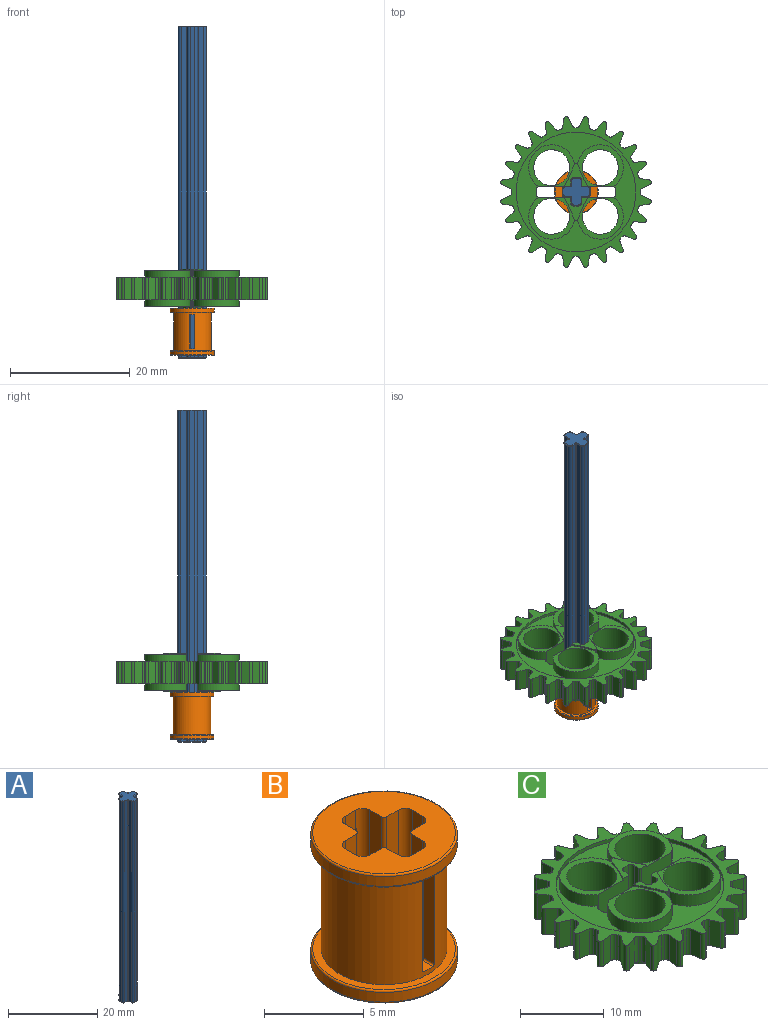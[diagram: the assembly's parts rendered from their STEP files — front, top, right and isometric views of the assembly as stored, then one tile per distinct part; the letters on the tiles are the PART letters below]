
ASSEMBLY  parts=3 mates=2
PART A: 74 faces, bbox 4.8x4.8x55.5 mm
  f0: cylinder r=0.1mm len=55.3mm, axis (0,0,-1), area 8.7mm2, adj f1,f23,f46,f70
  f1: plane 55.3x0.88mm, normal (1,0,0), area 48.4mm2, adj f0,f2,f44,f68
  f2: cylinder r=0.5mm len=55.3mm, axis (0,0,-1), area 43.4mm2, adj f1,f3,f42,f66
  f3: plane 55.3x0.75mm, normal (0,1,0), area 41.5mm2, adj f2,f4,f40,f64
  f4: cylinder r=0.5mm len=55.3mm, axis (0,0,-1), area 43.4mm2, adj f3,f5,f38,f62
  f5: plane 55.3x0.88mm, normal (-1,0,0), area 48.4mm2, adj f4,f6,f36,f60
  f6: cylinder r=0.1mm len=55.3mm, axis (0,0,-1), area 8.7mm2, adj f5,f7,f34,f58
  f7: plane 55.3x0.88mm, normal (0,1,0), area 48.4mm2, adj f6,f8,f32,f56
  f8: cylinder r=0.5mm len=55.3mm, axis (0,0,-1), area 43.4mm2, adj f7,f9,f30,f54
  f9: plane 55.3x0.75mm, normal (-1,0,0), area 41.5mm2, adj f8,f10,f28,f52
  f10: cylinder r=0.5mm len=55.3mm, axis (0,0,-1), area 43.4mm2, adj f9,f11,f26,f50
  f11: plane 55.3x0.88mm, normal (0,-1,0), area 48.4mm2, adj f10,f12,f27,f51
  f12: cylinder r=0.1mm len=55.3mm, axis (0,0,-1), area 8.7mm2, adj f11,f13,f29,f53
  f13: plane 55.3x0.88mm, normal (-1,0,0), area 48.4mm2, adj f12,f14,f31,f55
  f14: cylinder r=0.5mm len=55.3mm, axis (0,0,-1), area 43.4mm2, adj f13,f15,f33,f57
  f15: plane 55.3x0.75mm, normal (0,-1,0), area 41.5mm2, adj f14,f16,f35,f59
  f16: cylinder r=0.5mm len=55.3mm, axis (0,0,-1), area 43.4mm2, adj f15,f17,f37,f61
  f17: plane 55.3x0.88mm, normal (1,0,0), area 48.4mm2, adj f16,f18,f39,f63
  f18: cylinder r=0.1mm len=55.3mm, axis (0,0,-1), area 8.7mm2, adj f17,f19,f41,f65
  f19: plane 55.3x0.88mm, normal (0,-1,0), area 48.4mm2, adj f18,f20,f43,f67
  f20: cylinder r=0.5mm len=55.3mm, axis (0,0,-1), area 43.4mm2, adj f19,f21,f45,f69
  f21: plane 55.3x0.75mm, normal (1,0,0), area 41.5mm2, adj f20,f22,f47,f71
  f22: cylinder r=0.5mm len=55.3mm, axis (0,0,-1), area 43.4mm2, adj f21,f23,f49,f73
  f23: plane 55.3x0.88mm, normal (0,1,0), area 48.4mm2, adj f0,f22,f48,f72
  f24: plane 4.5x4.5mm, normal (0,0,1), area 11.3mm2, adj f50,f51,f52,f53,f54,f55,f56,f57
  f25: plane 4.5x4.5mm, normal (0,0,-1), area 11.3mm2, adj f26,f27,f28,f29,f30,f31,f32,f33
  f26: torus R=0.4mm, axis (0,0,1), area 0.1mm2, adj f10,f25,f27,f28
  f27: cylinder r=0.1mm len=0.88mm, axis (1,0,0), area 0.1mm2, adj f11,f25,f26,f29
  f28: cylinder r=0.1mm len=0.75mm, axis (0,-1,0), area 0.1mm2, adj f9,f25,f26,f30
  f29: torus R=0.2mm, axis (0,0,1), area 0mm2, adj f12,f25,f27,f31
  f30: torus R=0.4mm, axis (0,0,1), area 0.1mm2, adj f8,f25,f28,f32
  f31: cylinder r=0.1mm len=0.88mm, axis (0,-1,0), area 0.1mm2, adj f13,f25,f29,f33
  f32: cylinder r=0.1mm len=0.88mm, axis (-1,0,0), area 0.1mm2, adj f7,f25,f30,f34
  f33: torus R=0.4mm, axis (0,0,1), area 0.1mm2, adj f14,f25,f31,f35
  f34: torus R=0.2mm, axis (0,0,1), area 0mm2, adj f6,f25,f32,f36
  f35: cylinder r=0.1mm len=0.75mm, axis (1,0,0), area 0.1mm2, adj f15,f25,f33,f37
  f36: cylinder r=0.1mm len=0.88mm, axis (0,-1,0), area 0.1mm2, adj f5,f25,f34,f38
  f37: torus R=0.4mm, axis (0,0,1), area 0.1mm2, adj f16,f25,f35,f39
  f38: torus R=0.4mm, axis (0,0,1), area 0.1mm2, adj f4,f25,f36,f40
  f39: cylinder r=0.1mm len=0.88mm, axis (0,1,0), area 0.1mm2, adj f17,f25,f37,f41
  f40: cylinder r=0.1mm len=0.75mm, axis (-1,0,0), area 0.1mm2, adj f3,f25,f38,f42
  f41: torus R=0.2mm, axis (0,0,1), area 0mm2, adj f18,f25,f39,f43
  f42: torus R=0.4mm, axis (0,0,1), area 0.1mm2, adj f2,f25,f40,f44
  f43: cylinder r=0.1mm len=0.88mm, axis (1,0,0), area 0.1mm2, adj f19,f25,f41,f45
  f44: cylinder r=0.1mm len=0.88mm, axis (0,1,0), area 0.1mm2, adj f1,f25,f42,f46
  f45: torus R=0.4mm, axis (0,0,1), area 0.1mm2, adj f20,f25,f43,f47
  f46: torus R=0.2mm, axis (0,0,1), area 0mm2, adj f0,f25,f44,f48
  f47: cylinder r=0.1mm len=0.75mm, axis (0,1,0), area 0.1mm2, adj f21,f25,f45,f49
  f48: cylinder r=0.1mm len=0.88mm, axis (-1,0,0), area 0.1mm2, adj f23,f25,f46,f49
  f49: torus R=0.4mm, axis (0,0,1), area 0.1mm2, adj f22,f25,f47,f48
  f50: torus R=0.4mm, axis (0,0,1), area 0.1mm2, adj f10,f24,f51,f52
  f51: cylinder r=0.1mm len=0.88mm, axis (-1,0,0), area 0.1mm2, adj f11,f24,f50,f53
  f52: cylinder r=0.1mm len=0.75mm, axis (0,1,0), area 0.1mm2, adj f9,f24,f50,f54
  f53: torus R=0.2mm, axis (0,0,1), area 0mm2, adj f12,f24,f51,f55
  f54: torus R=0.4mm, axis (0,0,1), area 0.1mm2, adj f8,f24,f52,f56
  f55: cylinder r=0.1mm len=0.88mm, axis (0,1,0), area 0.1mm2, adj f13,f24,f53,f57
  f56: cylinder r=0.1mm len=0.88mm, axis (1,0,0), area 0.1mm2, adj f7,f24,f54,f58
  f57: torus R=0.4mm, axis (0,0,1), area 0.1mm2, adj f14,f24,f55,f59
  f58: torus R=0.2mm, axis (0,0,1), area 0mm2, adj f6,f24,f56,f60
  f59: cylinder r=0.1mm len=0.75mm, axis (-1,0,0), area 0.1mm2, adj f15,f24,f57,f61
  f60: cylinder r=0.1mm len=0.88mm, axis (0,1,0), area 0.1mm2, adj f5,f24,f58,f62
  f61: torus R=0.4mm, axis (0,0,1), area 0.1mm2, adj f16,f24,f59,f63
  f62: torus R=0.4mm, axis (0,0,1), area 0.1mm2, adj f4,f24,f60,f64
  f63: cylinder r=0.1mm len=0.88mm, axis (0,-1,0), area 0.1mm2, adj f17,f24,f61,f65
  f64: cylinder r=0.1mm len=0.75mm, axis (1,0,0), area 0.1mm2, adj f3,f24,f62,f66
  f65: torus R=0.2mm, axis (0,0,1), area 0mm2, adj f18,f24,f63,f67
  f66: torus R=0.4mm, axis (0,0,1), area 0.1mm2, adj f2,f24,f64,f68
  f67: cylinder r=0.1mm len=0.88mm, axis (-1,0,0), area 0.1mm2, adj f19,f24,f65,f69
  f68: cylinder r=0.1mm len=0.88mm, axis (0,-1,0), area 0.1mm2, adj f1,f24,f66,f70
  f69: torus R=0.4mm, axis (0,0,1), area 0.1mm2, adj f20,f24,f67,f71
  f70: torus R=0.2mm, axis (0,0,1), area 0mm2, adj f0,f24,f68,f72
  f71: cylinder r=0.1mm len=0.75mm, axis (0,-1,0), area 0.1mm2, adj f21,f24,f69,f73
  f72: cylinder r=0.1mm len=0.88mm, axis (1,0,0), area 0.1mm2, adj f23,f24,f70,f73
  f73: torus R=0.4mm, axis (0,0,1), area 0.1mm2, adj f22,f24,f71,f72
PART B: 53 faces, bbox 8x8x7.9 mm
  f0: plane 1.11x0.75mm, normal (0,1,0), area 0.8mm2, adj f13,f15,f30,f39,f40,f41
  f1: plane 1.11x0.75mm, normal (0,-1,0), area 0.8mm2, adj f25,f28,f30,f46,f47,f51
  f2: cylinder r=3.15mm len=6.3mm, axis (0,0,1), area 115mm2, adj f31,f32,f37,f38,f39,f40,f41,f42
  f3: cylinder r=3.67mm len=7.35mm, axis (0,0,-1), area 13.9mm2, adj f34,f35
  f4: plane 7.9x0.8mm, normal (-1,0,0), area 6.3mm2, adj f5,f28,f29,f30
  f5: cylinder r=0.2mm len=7.9mm, axis (0,0,-1), area 2.5mm2, adj f4,f6,f29,f30
  f6: plane 7.9x0.8mm, normal (0,-1,0), area 6.3mm2, adj f5,f7,f29,f30
  f7: cylinder r=0.5mm len=7.9mm, axis (0,0,-1), area 6.2mm2, adj f6,f8,f29,f30
  f8: plane 7.9x0.75mm, normal (-1,0,0), area 5.9mm2, adj f7,f9,f29,f30
  f9: cylinder r=0.5mm len=7.9mm, axis (0,0,-1), area 6.2mm2, adj f8,f10,f29,f30
  f10: plane 7.9x0.8mm, normal (0,1,0), area 6.3mm2, adj f9,f11,f29,f30
  f11: cylinder r=0.2mm len=7.9mm, axis (0,0,-1), area 2.5mm2, adj f10,f12,f29,f30
  f12: plane 7.9x0.8mm, normal (-1,0,0), area 6.3mm2, adj f11,f13,f29,f30
  f13: cylinder r=0.5mm len=7.9mm, axis (0,0,-1), area 5.9mm2, adj f0,f12,f14,f29,f30,f37,f38,f39
  f14: plane 1.11x0.75mm, normal (0,1,0), area 0.8mm2, adj f13,f15,f29,f37,f43,f44
  f15: cylinder r=0.5mm len=7.9mm, axis (0,0,-1), area 5.9mm2, adj f0,f14,f16,f29,f30,f41,f42,f43
  f16: plane 7.9x0.8mm, normal (1,0,0), area 6.3mm2, adj f15,f17,f29,f30
  f17: cylinder r=0.2mm len=7.9mm, axis (0,0,-1), area 2.5mm2, adj f16,f18,f29,f30
  f18: plane 7.9x0.8mm, normal (0,1,0), area 6.3mm2, adj f17,f19,f29,f30
  f19: cylinder r=0.5mm len=7.9mm, axis (0,0,-1), area 6.2mm2, adj f18,f20,f29,f30
  f20: plane 7.9x0.75mm, normal (1,0,0), area 5.9mm2, adj f19,f21,f29,f30
  f21: cylinder r=0.5mm len=7.9mm, axis (0,0,-1), area 6.2mm2, adj f20,f22,f29,f30
  f22: plane 7.9x0.8mm, normal (0,-1,0), area 6.3mm2, adj f21,f23,f29,f30
  f23: cylinder r=0.2mm len=7.9mm, axis (0,0,-1), area 2.5mm2, adj f22,f24,f29,f30
  f24: plane 7.9x0.8mm, normal (1,0,0), area 6.3mm2, adj f23,f25,f29,f30
  f25: cylinder r=0.5mm len=7.9mm, axis (0,0,-1), area 5.9mm2, adj f1,f24,f26,f29,f30,f49,f50,f51
  f26: plane 1.11x0.75mm, normal (0,-1,0), area 0.8mm2, adj f25,f28,f29,f45,f48,f49
  f27: cylinder r=3.67mm len=7.35mm, axis (0,0,-1), area 13.9mm2, adj f33,f36
  f28: cylinder r=0.5mm len=7.9mm, axis (0,0,-1), area 5.9mm2, adj f1,f4,f26,f29,f30,f47,f48,f52
  f29: plane 7.15x7.15mm, normal (0,0,1), area 27mm2, adj f4,f5,f6,f7,f8,f9,f10,f11
  f30: plane 7.15x7.15mm, normal (0,0,-1), area 27mm2, adj f0,f1,f4,f5,f6,f7,f8,f9
  f31: plane 7.15x7.15mm, normal (0,0,-1), area 9mm2, adj f2,f33
  f32: plane 7.15x7.15mm, normal (0,0,1), area 9mm2, adj f2,f34
  f33: torus R=3.58mm, axis (0,0,1), area 3.6mm2, adj f27,f31
  f34: torus R=3.58mm, axis (0,0,1), area 3.6mm2, adj f3,f32
  f35: torus R=3.58mm, axis (0,0,1), area 3.6mm2, adj f3,f30
  f36: torus R=3.58mm, axis (0,0,1), area 3.6mm2, adj f27,f29
  f37: cylinder r=0.1mm len=0.76mm, axis (0,-1,0), area 0.1mm2, adj f2,f13,f14,f38,f44
  f38: plane 5.5x0.75mm, normal (-1,0,0), area 4.1mm2, adj f2,f13,f37,f39
  f39: cylinder r=0.1mm len=0.76mm, axis (0,-1,0), area 0.1mm2, adj f0,f2,f13,f38,f40
  f40: plane 0.78x0.65mm, normal (0,0,1), area 0.5mm2, adj f0,f2,f39,f41
  f41: cylinder r=0.1mm len=0.76mm, axis (0,-1,0), area 0.1mm2, adj f0,f2,f15,f40,f42
  f42: plane 5.5x0.75mm, normal (1,0,0), area 4.1mm2, adj f2,f15,f41,f43
  f43: cylinder r=0.1mm len=0.76mm, axis (0,-1,0), area 0.1mm2, adj f2,f14,f15,f42,f44
  f44: plane 0.78x0.65mm, normal (0,0,-1), area 0.5mm2, adj f2,f14,f37,f43
  f45: plane 0.78x0.65mm, normal (0,0,-1), area 0.5mm2, adj f2,f26,f48,f49
  f46: plane 0.78x0.65mm, normal (0,0,1), area 0.5mm2, adj f1,f2,f47,f51
  f47: cylinder r=0.1mm len=0.76mm, axis (0,-1,0), area 0.1mm2, adj f1,f2,f28,f46,f52
  f48: cylinder r=0.1mm len=0.76mm, axis (0,-1,0), area 0.1mm2, adj f2,f26,f28,f45,f52
  f49: cylinder r=0.1mm len=0.76mm, axis (0,-1,0), area 0.1mm2, adj f2,f25,f26,f45,f50
  f50: plane 5.5x0.75mm, normal (1,0,0), area 4.1mm2, adj f2,f25,f49,f51
  f51: cylinder r=0.1mm len=0.76mm, axis (0,-1,0), area 0.1mm2, adj f1,f2,f25,f46,f50
  f52: plane 5.5x0.75mm, normal (-1,0,0), area 4.1mm2, adj f2,f28,f47,f48
PART C: 242 faces, bbox 25.3x25.3x6.5 mm
  f0: plane 7.61x7.02mm, normal (0,0,-1), area 14.5mm2, adj f4,f189,f190,f212,f222,f228
  f1: plane 7.61x7.02mm, normal (0,0,1), area 14.5mm2, adj f3,f190,f191,f203,f222,f228
  f2: plane 3.93x3.88mm, normal (0,0,1), area 5.4mm2, adj f3,f199,f202,f203,f206,f224,f225,f226
  f3: cylinder r=20mm len=3.7mm, axis (0,0,-1), area 1mm2, adj f1,f2,f203,f228
  f4: cylinder r=20mm len=3.7mm, axis (0,0,-1), area 1mm2, adj f0,f5,f212,f228
  f5: plane 3.93x3.88mm, normal (0,0,-1), area 5.4mm2, adj f4,f209,f210,f211,f212,f224,f225,f226
  f6: plane 20x20mm, normal (0,0,1), area 104.2mm2, adj f12,f17,f188,f191,f196,f199,f201,f203
  f7: plane 20x20mm, normal (0,0,-1), area 104.2mm2, adj f11,f16,f186,f189,f194,f208,f209,f211
  f8: plane 7.61x7.02mm, normal (0,0,-1), area 14.5mm2, adj f186,f187,f210,f211,f221,f238
  f9: plane 7.61x7.02mm, normal (0,0,1), area 14.5mm2, adj f187,f188,f199,f202,f221,f238
  f10: plane 7.61x7.02mm, normal (0,0,-1), area 14.5mm2, adj f11,f192,f213,f214,f220,f229
  f11: cylinder r=3.82mm len=7.61mm, axis (0,0,-1), area 24.7mm2, adj f7,f10,f214,f220
  f12: cylinder r=3.82mm len=7.61mm, axis (0,0,-1), area 24.7mm2, adj f6,f13,f204,f220
  f13: plane 7.61x7.02mm, normal (0,0,1), area 14.5mm2, adj f12,f192,f204,f205,f220,f229
  f14: plane 25.27x25.27mm, normal (0,0,1), area 106.3mm2, adj f17,f18,f19,f20,f21,f22,f23,f24
  f15: plane 25.27x25.27mm, normal (0,0,-1), area 106.3mm2, adj f16,f18,f19,f20,f21,f22,f23,f24
  f16: cylinder r=10mm len=20mm, axis (0,0,-1), area 31.4mm2, adj f7,f15
  f17: cylinder r=10mm len=20mm, axis (0,0,-1), area 31.4mm2, adj f6,f14
  f18: cylinder r=0.5mm len=3.75mm, axis (0,0,1), area 2.1mm2, adj f14,f15,f19,f185
  f19: cylinder r=0.5mm len=3.75mm, axis (0,0,1), area 2.1mm2, adj f14,f15,f18,f20
  f20: plane 3.75x1.41mm, normal (0.99,0.16,0), area 5.3mm2, adj f14,f15,f19,f21
  f21: cylinder r=0.5mm len=3.75mm, axis (0,0,1), area 2.1mm2, adj f14,f15,f20,f22
  f22: plane 3.75x0.34mm, normal (0.26,0.97,0), area 1.3mm2, adj f14,f15,f21,f23
  f23: cylinder r=0.5mm len=3.75mm, axis (0,0,1), area 2.1mm2, adj f14,f15,f22,f24
  f24: plane 3.75x1.1mm, normal (-0.77,0.64,0), area 5.3mm2, adj f14,f15,f23,f25
  f25: cylinder r=0.5mm len=3.75mm, axis (0,0,1), area 2.1mm2, adj f14,f15,f24,f26
  f26: cylinder r=0.5mm len=3.75mm, axis (0,0,1), area 2.1mm2, adj f14,f15,f25,f27
  f27: plane 3.75x1.42mm, normal (1,-0.1,0), area 5.3mm2, adj f14,f15,f26,f28
  f28: cylinder r=0.5mm len=3.75mm, axis (0,0,1), area 2.1mm2, adj f14,f15,f27,f29
  f29: plane 3.75x0.31mm, normal (0.5,0.87,0), area 1.3mm2, adj f14,f15,f28,f30
  f30: cylinder r=0.5mm len=3.75mm, axis (0,0,1), area 2.1mm2, adj f14,f15,f29,f31
  f31: plane 3.75x1.16mm, normal (-0.58,0.81,0), area 5.3mm2, adj f14,f15,f30,f32
  f32: cylinder r=0.5mm len=3.75mm, axis (0,0,1), area 2.1mm2, adj f14,f15,f31,f33
  f33: cylinder r=0.5mm len=3.75mm, axis (0,0,1), area 2.1mm2, adj f14,f15,f32,f34
  f34: plane 3.75x1.34mm, normal (0.94,-0.35,0), area 5.3mm2, adj f14,f15,f33,f35
  f35: cylinder r=0.5mm len=3.75mm, axis (0,0,1), area 2.1mm2, adj f14,f15,f34,f36
  f36: plane 3.75x0.25mm, normal (0.71,0.71,0), area 1.3mm2, adj f14,f15,f35,f37
  f37: cylinder r=0.5mm len=3.75mm, axis (0,0,1), area 2.1mm2, adj f14,f15,f36,f38
  f38: plane 3.75x1.34mm, normal (-0.35,0.94,0), area 5.3mm2, adj f14,f15,f37,f39
  f39: cylinder r=0.5mm len=3.75mm, axis (0,0,1), area 2.1mm2, adj f14,f15,f38,f40
  f40: cylinder r=0.5mm len=3.75mm, axis (0,0,1), area 2.1mm2, adj f14,f15,f39,f41
  f41: plane 3.75x1.16mm, normal (0.81,-0.58,0), area 5.3mm2, adj f14,f15,f40,f42
  f42: cylinder r=0.5mm len=3.75mm, axis (0,0,1), area 2.1mm2, adj f14,f15,f41,f43
  f43: plane 3.75x0.31mm, normal (0.87,0.5,0), area 1.3mm2, adj f14,f15,f42,f44
  f44: cylinder r=0.5mm len=3.75mm, axis (0,0,1), area 2.1mm2, adj f14,f15,f43,f45
  f45: plane 3.75x1.42mm, normal (-0.1,1,0), area 5.3mm2, adj f14,f15,f44,f46
  f46: cylinder r=0.5mm len=3.75mm, axis (0,0,1), area 2.1mm2, adj f14,f15,f45,f47
  f47: cylinder r=0.5mm len=3.75mm, axis (0,0,1), area 2.1mm2, adj f14,f15,f46,f48
  f48: plane 3.75x1.1mm, normal (0.64,-0.77,0), area 5.3mm2, adj f14,f15,f47,f49
  f49: cylinder r=0.5mm len=3.75mm, axis (0,0,1), area 2.1mm2, adj f14,f15,f48,f50
  f50: plane 3.75x0.34mm, normal (0.97,0.26,0), area 1.3mm2, adj f14,f15,f49,f51
  f51: cylinder r=0.5mm len=3.75mm, axis (0,0,1), area 2.1mm2, adj f14,f15,f50,f52
  f52: plane 3.75x1.41mm, normal (0.16,0.99,0), area 5.3mm2, adj f14,f15,f51,f53
  f53: cylinder r=0.5mm len=3.75mm, axis (0,0,1), area 2.1mm2, adj f14,f15,f52,f54
  f54: cylinder r=0.5mm len=3.75mm, axis (0,0,1), area 2.1mm2, adj f14,f15,f53,f55
  f55: plane 3.75x1.3mm, normal (0.41,-0.91,0), area 5.3mm2, adj f14,f15,f54,f56
  f56: cylinder r=0.5mm len=3.75mm, axis (0,0,1), area 2.1mm2, adj f14,f15,f55,f57
  f57: plane 3.75x0.36mm, normal (1,0,0), area 1.3mm2, adj f14,f15,f56,f58
  f58: cylinder r=0.5mm len=3.75mm, axis (0,0,1), area 2.1mm2, adj f14,f15,f57,f59
  f59: plane 3.75x1.3mm, normal (0.41,0.91,0), area 5.3mm2, adj f14,f15,f58,f60
  f60: cylinder r=0.5mm len=3.75mm, axis (0,0,1), area 2.1mm2, adj f14,f15,f59,f61
  f61: cylinder r=0.5mm len=3.75mm, axis (0,0,1), area 2.1mm2, adj f14,f15,f60,f62
  f62: plane 3.75x1.41mm, normal (0.16,-0.99,0), area 5.3mm2, adj f14,f15,f61,f63
  f63: cylinder r=0.5mm len=3.75mm, axis (0,0,1), area 2.1mm2, adj f14,f15,f62,f64
  f64: plane 3.75x0.34mm, normal (0.97,-0.26,0), area 1.3mm2, adj f14,f15,f63,f65
  f65: cylinder r=0.5mm len=3.75mm, axis (0,0,1), area 2.1mm2, adj f14,f15,f64,f66
  f66: plane 3.75x1.1mm, normal (0.64,0.77,0), area 5.3mm2, adj f14,f15,f65,f67
  f67: cylinder r=0.5mm len=3.75mm, axis (0,0,1), area 2.1mm2, adj f14,f15,f66,f68
  f68: cylinder r=0.5mm len=3.75mm, axis (0,0,1), area 2.1mm2, adj f14,f15,f67,f69
  f69: plane 3.75x1.42mm, normal (-0.1,-1,0), area 5.3mm2, adj f14,f15,f68,f70
  f70: cylinder r=0.5mm len=3.75mm, axis (0,0,1), area 2.1mm2, adj f14,f15,f69,f71
  f71: plane 3.75x0.31mm, normal (0.87,-0.5,0), area 1.3mm2, adj f14,f15,f70,f72
  f72: cylinder r=0.5mm len=3.75mm, axis (0,0,1), area 2.1mm2, adj f14,f15,f71,f73
  f73: plane 3.75x1.16mm, normal (0.81,0.58,0), area 5.3mm2, adj f14,f15,f72,f74
  f74: cylinder r=0.5mm len=3.75mm, axis (0,0,1), area 2.1mm2, adj f14,f15,f73,f75
  f75: cylinder r=0.5mm len=3.75mm, axis (0,0,1), area 2.1mm2, adj f14,f15,f74,f76
  f76: plane 3.75x1.34mm, normal (-0.35,-0.94,0), area 5.3mm2, adj f14,f15,f75,f77
  f77: cylinder r=0.5mm len=3.75mm, axis (0,0,1), area 2.1mm2, adj f14,f15,f76,f78
  f78: plane 3.75x0.25mm, normal (0.71,-0.71,0), area 1.3mm2, adj f14,f15,f77,f79
  f79: cylinder r=0.5mm len=3.75mm, axis (0,0,1), area 2.1mm2, adj f14,f15,f78,f80
  f80: plane 3.75x1.34mm, normal (0.94,0.35,0), area 5.3mm2, adj f14,f15,f79,f81
  f81: cylinder r=0.5mm len=3.75mm, axis (0,0,1), area 2.1mm2, adj f14,f15,f80,f82
  f82: cylinder r=0.5mm len=3.75mm, axis (0,0,1), area 2.1mm2, adj f14,f15,f81,f83
  f83: plane 3.75x1.16mm, normal (-0.58,-0.81,0), area 5.3mm2, adj f14,f15,f82,f84
  f84: cylinder r=0.5mm len=3.75mm, axis (0,0,1), area 2.1mm2, adj f14,f15,f83,f85
  f85: plane 3.75x0.31mm, normal (0.5,-0.87,0), area 1.3mm2, adj f14,f15,f84,f86
  f86: cylinder r=0.5mm len=3.75mm, axis (0,0,1), area 2.1mm2, adj f14,f15,f85,f87
  f87: plane 3.75x1.42mm, normal (1,0.1,0), area 5.3mm2, adj f14,f15,f86,f88
  f88: cylinder r=0.5mm len=3.75mm, axis (0,0,1), area 2.1mm2, adj f14,f15,f87,f89
  f89: cylinder r=0.5mm len=3.75mm, axis (0,0,1), area 2.1mm2, adj f14,f15,f88,f90
  f90: plane 3.75x1.1mm, normal (-0.77,-0.64,0), area 5.3mm2, adj f14,f15,f89,f91
  f91: cylinder r=0.5mm len=3.75mm, axis (0,0,1), area 2.1mm2, adj f14,f15,f90,f92
  f92: plane 3.75x0.34mm, normal (0.26,-0.97,0), area 1.3mm2, adj f14,f15,f91,f93
  f93: cylinder r=0.5mm len=3.75mm, axis (0,0,1), area 2.1mm2, adj f14,f15,f92,f94
  f94: plane 3.75x1.41mm, normal (0.99,-0.16,0), area 5.3mm2, adj f14,f15,f93,f95
  f95: cylinder r=0.5mm len=3.75mm, axis (0,0,1), area 2.1mm2, adj f14,f15,f94,f96
  f96: cylinder r=0.5mm len=3.75mm, axis (0,0,1), area 2.1mm2, adj f14,f15,f95,f97
  f97: plane 3.75x1.3mm, normal (-0.91,-0.41,0), area 5.3mm2, adj f14,f15,f96,f98
  f98: cylinder r=0.5mm len=3.75mm, axis (0,0,1), area 2.1mm2, adj f14,f15,f97,f99
  f99: plane 3.75x0.36mm, normal (0,-1,0), area 1.3mm2, adj f14,f15,f98,f100
  f100: cylinder r=0.5mm len=3.75mm, axis (0,0,1), area 2.1mm2, adj f14,f15,f99,f101
  f101: plane 3.75x1.3mm, normal (0.91,-0.41,0), area 5.3mm2, adj f14,f15,f100,f102
  f102: cylinder r=0.5mm len=3.75mm, axis (0,0,1), area 2.1mm2, adj f14,f15,f101,f103
  f103: cylinder r=0.5mm len=3.75mm, axis (0,0,1), area 2.1mm2, adj f14,f15,f102,f104
  f104: plane 3.75x1.41mm, normal (-0.99,-0.16,0), area 5.3mm2, adj f14,f15,f103,f105
  f105: cylinder r=0.5mm len=3.75mm, axis (0,0,1), area 2.1mm2, adj f14,f15,f104,f106
  f106: plane 3.75x0.34mm, normal (-0.26,-0.97,0), area 1.3mm2, adj f14,f15,f105,f107
  f107: cylinder r=0.5mm len=3.75mm, axis (0,0,1), area 2.1mm2, adj f14,f15,f106,f108
  f108: plane 3.75x1.1mm, normal (0.77,-0.64,0), area 5.3mm2, adj f14,f15,f107,f109
  f109: cylinder r=0.5mm len=3.75mm, axis (0,0,1), area 2.1mm2, adj f14,f15,f108,f110
  f110: cylinder r=0.5mm len=3.75mm, axis (0,0,1), area 2.1mm2, adj f14,f15,f109,f111
  f111: plane 3.75x1.42mm, normal (-1,0.1,0), area 5.3mm2, adj f14,f15,f110,f112
  f112: cylinder r=0.5mm len=3.75mm, axis (0,0,1), area 2.1mm2, adj f14,f15,f111,f113
  f113: plane 3.75x0.31mm, normal (-0.5,-0.87,0), area 1.3mm2, adj f14,f15,f112,f114
  f114: cylinder r=0.5mm len=3.75mm, axis (0,0,1), area 2.1mm2, adj f14,f15,f113,f115
  f115: plane 3.75x1.16mm, normal (0.58,-0.81,0), area 5.3mm2, adj f14,f15,f114,f116
  f116: cylinder r=0.5mm len=3.75mm, axis (0,0,1), area 2.1mm2, adj f14,f15,f115,f117
  f117: cylinder r=0.5mm len=3.75mm, axis (0,0,1), area 2.1mm2, adj f14,f15,f116,f118
  f118: plane 3.75x1.34mm, normal (-0.94,0.35,0), area 5.3mm2, adj f14,f15,f117,f119
  f119: cylinder r=0.5mm len=3.75mm, axis (0,0,1), area 2.1mm2, adj f14,f15,f118,f120
  f120: plane 3.75x0.25mm, normal (-0.71,-0.71,0), area 1.3mm2, adj f14,f15,f119,f121
  f121: cylinder r=0.5mm len=3.75mm, axis (0,0,1), area 2.1mm2, adj f14,f15,f120,f122
  f122: plane 3.75x1.34mm, normal (0.35,-0.94,0), area 5.3mm2, adj f14,f15,f121,f123
  f123: cylinder r=0.5mm len=3.75mm, axis (0,0,1), area 2.1mm2, adj f14,f15,f122,f124
  f124: cylinder r=0.5mm len=3.75mm, axis (0,0,1), area 2.1mm2, adj f14,f15,f123,f125
  f125: plane 3.75x1.16mm, normal (-0.81,0.58,0), area 5.3mm2, adj f14,f15,f124,f126
  f126: cylinder r=0.5mm len=3.75mm, axis (0,0,1), area 2.1mm2, adj f14,f15,f125,f127
  f127: plane 3.75x0.31mm, normal (-0.87,-0.5,0), area 1.3mm2, adj f14,f15,f126,f128
  f128: cylinder r=0.5mm len=3.75mm, axis (0,0,1), area 2.1mm2, adj f14,f15,f127,f129
  f129: plane 3.75x1.42mm, normal (0.1,-1,0), area 5.3mm2, adj f14,f15,f128,f130
  f130: cylinder r=0.5mm len=3.75mm, axis (0,0,1), area 2.1mm2, adj f14,f15,f129,f131
  f131: cylinder r=0.5mm len=3.75mm, axis (0,0,1), area 2.1mm2, adj f14,f15,f130,f132
  f132: plane 3.75x1.1mm, normal (-0.64,0.77,0), area 5.3mm2, adj f14,f15,f131,f133
  f133: cylinder r=0.5mm len=3.75mm, axis (0,0,1), area 2.1mm2, adj f14,f15,f132,f134
  f134: plane 3.75x0.34mm, normal (-0.97,-0.26,0), area 1.3mm2, adj f14,f15,f133,f135
  f135: cylinder r=0.5mm len=3.75mm, axis (0,0,1), area 2.1mm2, adj f14,f15,f134,f136
  f136: plane 3.75x1.41mm, normal (-0.16,-0.99,0), area 5.3mm2, adj f14,f15,f135,f137
  f137: cylinder r=0.5mm len=3.75mm, axis (0,0,1), area 2.1mm2, adj f14,f15,f136,f138
  f138: cylinder r=0.5mm len=3.75mm, axis (0,0,1), area 2.1mm2, adj f14,f15,f137,f139
  f139: plane 3.75x1.3mm, normal (-0.41,0.91,0), area 5.3mm2, adj f14,f15,f138,f140
  f140: cylinder r=0.5mm len=3.75mm, axis (0,0,1), area 2.1mm2, adj f14,f15,f139,f141
  f141: plane 3.75x0.36mm, normal (-1,0,0), area 1.3mm2, adj f14,f15,f140,f142
  f142: cylinder r=0.5mm len=3.75mm, axis (0,0,1), area 2.1mm2, adj f14,f15,f141,f143
  f143: plane 3.75x1.3mm, normal (-0.41,-0.91,0), area 5.3mm2, adj f14,f15,f142,f144
  f144: cylinder r=0.5mm len=3.75mm, axis (0,0,1), area 2.1mm2, adj f14,f15,f143,f145
  f145: cylinder r=0.5mm len=3.75mm, axis (0,0,1), area 2.1mm2, adj f14,f15,f144,f146
  f146: plane 3.75x1.41mm, normal (-0.16,0.99,0), area 5.3mm2, adj f14,f15,f145,f147
  f147: cylinder r=0.5mm len=3.75mm, axis (0,0,1), area 2.1mm2, adj f14,f15,f146,f148
  f148: plane 3.75x0.34mm, normal (-0.97,0.26,0), area 1.3mm2, adj f14,f15,f147,f149
  f149: cylinder r=0.5mm len=3.75mm, axis (0,0,1), area 2.1mm2, adj f14,f15,f148,f150
  f150: plane 3.75x1.1mm, normal (-0.64,-0.77,0), area 5.3mm2, adj f14,f15,f149,f151
  f151: cylinder r=0.5mm len=3.75mm, axis (0,0,1), area 2.1mm2, adj f14,f15,f150,f152
  f152: cylinder r=0.5mm len=3.75mm, axis (0,0,1), area 2.1mm2, adj f14,f15,f151,f153
  f153: plane 3.75x1.42mm, normal (0.1,1,0), area 5.3mm2, adj f14,f15,f152,f154
  f154: cylinder r=0.5mm len=3.75mm, axis (0,0,1), area 2.1mm2, adj f14,f15,f153,f155
  f155: plane 3.75x0.31mm, normal (-0.87,0.5,0), area 1.3mm2, adj f14,f15,f154,f156
  f156: cylinder r=0.5mm len=3.75mm, axis (0,0,1), area 2.1mm2, adj f14,f15,f155,f157
  f157: plane 3.75x1.16mm, normal (-0.81,-0.58,0), area 5.3mm2, adj f14,f15,f156,f158
  f158: cylinder r=0.5mm len=3.75mm, axis (0,0,1), area 2.1mm2, adj f14,f15,f157,f159
  f159: cylinder r=0.5mm len=3.75mm, axis (0,0,1), area 2.1mm2, adj f14,f15,f158,f160
  f160: plane 3.75x1.34mm, normal (0.35,0.94,0), area 5.3mm2, adj f14,f15,f159,f161
  f161: cylinder r=0.5mm len=3.75mm, axis (0,0,1), area 2.1mm2, adj f14,f15,f160,f162
  f162: plane 3.75x0.25mm, normal (-0.71,0.71,0), area 1.3mm2, adj f14,f15,f161,f163
  f163: cylinder r=0.5mm len=3.75mm, axis (0,0,1), area 2.1mm2, adj f14,f15,f162,f164
  f164: plane 3.75x1.34mm, normal (-0.94,-0.35,0), area 5.3mm2, adj f14,f15,f163,f165
  f165: cylinder r=0.5mm len=3.75mm, axis (0,0,1), area 2.1mm2, adj f14,f15,f164,f166
  f166: cylinder r=0.5mm len=3.75mm, axis (0,0,1), area 2.1mm2, adj f14,f15,f165,f167
  f167: plane 3.75x1.16mm, normal (0.58,0.81,0), area 5.3mm2, adj f14,f15,f166,f168
  f168: cylinder r=0.5mm len=3.75mm, axis (0,0,1), area 2.1mm2, adj f14,f15,f167,f169
  f169: plane 3.75x0.31mm, normal (-0.5,0.87,0), area 1.3mm2, adj f14,f15,f168,f170
  f170: cylinder r=0.5mm len=3.75mm, axis (0,0,1), area 2.1mm2, adj f14,f15,f169,f171
  f171: plane 3.75x1.42mm, normal (-1,-0.1,0), area 5.3mm2, adj f14,f15,f170,f172
  f172: cylinder r=0.5mm len=3.75mm, axis (0,0,1), area 2.1mm2, adj f14,f15,f171,f173
  f173: cylinder r=0.5mm len=3.75mm, axis (0,0,1), area 2.1mm2, adj f14,f15,f172,f174
  f174: plane 3.75x1.1mm, normal (0.77,0.64,0), area 5.3mm2, adj f14,f15,f173,f175
  f175: cylinder r=0.5mm len=3.75mm, axis (0,0,1), area 2.1mm2, adj f14,f15,f174,f176
  f176: plane 3.75x0.34mm, normal (-0.26,0.97,0), area 1.3mm2, adj f14,f15,f175,f177
  f177: cylinder r=0.5mm len=3.75mm, axis (0,0,1), area 2.1mm2, adj f14,f15,f176,f178
  f178: plane 3.75x1.41mm, normal (-0.99,0.16,0), area 5.3mm2, adj f14,f15,f177,f179
  f179: cylinder r=0.5mm len=3.75mm, axis (0,0,1), area 2.1mm2, adj f14,f15,f178,f180
  f180: cylinder r=0.5mm len=3.75mm, axis (0,0,1), area 2.1mm2, adj f14,f15,f179,f181
  f181: plane 3.75x1.3mm, normal (0.91,0.41,0), area 5.3mm2, adj f14,f15,f180,f182
  f182: cylinder r=0.5mm len=3.75mm, axis (0,0,1), area 2.1mm2, adj f14,f15,f181,f183
  f183: plane 3.75x0.36mm, normal (0,1,0), area 1.3mm2, adj f14,f15,f182,f184
  f184: cylinder r=0.5mm len=3.75mm, axis (0,0,1), area 2.1mm2, adj f14,f15,f183,f185
  f185: plane 3.75x1.3mm, normal (-0.91,0.41,0), area 5.3mm2, adj f14,f15,f18,f184
  f186: cylinder r=3.82mm len=7.61mm, axis (0,0,-1), area 24.7mm2, adj f7,f8,f211,f221
  f187: cylinder r=3mm len=6mm, axis (0,0,-1), area 113.1mm2, adj f8,f9
  f188: cylinder r=3.82mm len=7.61mm, axis (0,0,-1), area 24.7mm2, adj f6,f9,f199,f221
  f189: cylinder r=3.82mm len=7.61mm, axis (0,0,-1), area 24.7mm2, adj f0,f7,f212,f222
  f190: cylinder r=3mm len=6mm, axis (0,0,-1), area 113.1mm2, adj f0,f1
  f191: cylinder r=3.82mm len=7.61mm, axis (0,0,-1), area 24.7mm2, adj f1,f6,f203,f222
  f192: cylinder r=3mm len=6mm, axis (0,0,-1), area 113.1mm2, adj f10,f13
  f193: plane 7.61x7.02mm, normal (0,0,-1), area 14.5mm2, adj f194,f195,f215,f216,f223,f237
  f194: cylinder r=3.82mm len=7.61mm, axis (0,0,-1), area 24.7mm2, adj f7,f193,f215,f223
  f195: cylinder r=3mm len=6mm, axis (0,0,-1), area 113.1mm2, adj f193,f197
  f196: cylinder r=3.82mm len=7.61mm, axis (0,0,-1), area 24.7mm2, adj f6,f197,f201,f223
  f197: plane 7.61x7.02mm, normal (0,0,1), area 14.5mm2, adj f195,f196,f200,f201,f223,f237
  f198: plane 3.93x3.88mm, normal (0,0,1), area 5.4mm2, adj f200,f201,f204,f205,f207,f229,f230,f231
  f199: cylinder r=0.25mm len=1.88mm, axis (0,0,-1), area 0.5mm2, adj f2,f6,f9,f188,f202,f206
  f200: cylinder r=20mm len=3.7mm, axis (0,0,-1), area 1mm2, adj f197,f198,f201,f237
  f201: cylinder r=0.25mm len=1.88mm, axis (0,0,-1), area 0.5mm2, adj f6,f196,f197,f198,f200,f207
  f202: cylinder r=20mm len=3.7mm, axis (0,0,-1), area 1mm2, adj f2,f9,f199,f238
  f203: cylinder r=0.25mm len=1.88mm, axis (0,0,-1), area 0.5mm2, adj f1,f2,f3,f6,f191,f206
  f204: cylinder r=0.25mm len=1.88mm, axis (0,0,-1), area 0.5mm2, adj f6,f12,f13,f198,f205,f207
  f205: cylinder r=20mm len=3.7mm, axis (0,0,-1), area 1mm2, adj f13,f198,f204,f229
  f206: plane 1.88x0.14mm, normal (0,1,0), area 0.3mm2, adj f2,f6,f199,f203
  f207: plane 1.88x0.14mm, normal (0,-1,0), area 0.3mm2, adj f6,f198,f201,f204
  f208: plane 1.88x0.14mm, normal (0,-1,0), area 0.3mm2, adj f7,f214,f215,f217
  f209: plane 1.88x0.14mm, normal (0,1,0), area 0.3mm2, adj f5,f7,f211,f212
  f210: cylinder r=20mm len=3.7mm, axis (0,0,-1), area 1mm2, adj f5,f8,f211,f238
  f211: cylinder r=0.25mm len=1.88mm, axis (0,0,-1), area 0.5mm2, adj f5,f7,f8,f186,f209,f210
  f212: cylinder r=0.25mm len=1.88mm, axis (0,0,-1), area 0.5mm2, adj f0,f4,f5,f7,f189,f209
  f213: cylinder r=20mm len=3.7mm, axis (0,0,-1), area 1mm2, adj f10,f214,f217,f229
  f214: cylinder r=0.25mm len=1.88mm, axis (0,0,-1), area 0.5mm2, adj f7,f10,f11,f208,f213,f217
  f215: cylinder r=0.25mm len=1.88mm, axis (0,0,-1), area 0.5mm2, adj f7,f193,f194,f208,f216,f217
  f216: cylinder r=20mm len=3.7mm, axis (0,0,-1), area 1mm2, adj f193,f215,f217,f237
  f217: plane 3.93x3.88mm, normal (0,0,-1), area 5.4mm2, adj f208,f213,f214,f215,f216,f229,f230,f231
  f218: plane 2.75x0.75mm, normal (1,0,0), area 2.1mm2, adj f6,f7,f220,f222
  f219: plane 2.75x0.75mm, normal (-1,0,0), area 2.1mm2, adj f6,f7,f221,f223
  f220: cylinder r=0.5mm len=6mm, axis (0,0,1), area 2.2mm2, adj f6,f7,f10,f11,f12,f13,f218,f229
  f221: cylinder r=0.5mm len=6mm, axis (0,0,1), area 2.2mm2, adj f6,f7,f8,f9,f186,f188,f219,f238
  f222: cylinder r=0.5mm len=6mm, axis (0,0,1), area 2.2mm2, adj f0,f1,f6,f7,f189,f191,f218,f228
  f223: cylinder r=0.5mm len=6mm, axis (0,0,1), area 2.2mm2, adj f6,f7,f193,f194,f196,f197,f219,f237
  f224: plane 6.5x0.75mm, normal (0,-1,0), area 4.9mm2, adj f2,f5,f225,f241
  f225: cylinder r=0.5mm len=6.5mm, axis (0,0,1), area 5.1mm2, adj f2,f5,f224,f226
  f226: plane 6.5x0.8mm, normal (1,0,0), area 5.2mm2, adj f2,f5,f225,f227
  f227: cylinder r=0.2mm len=6.5mm, axis (0,0,1), area 2mm2, adj f2,f5,f226,f228
  f228: plane 6.5x5.09mm, normal (0,-1,0), area 31mm2, adj f0,f1,f2,f3,f4,f5,f222,f227
  f229: plane 6.5x5.09mm, normal (0,1,0), area 31mm2, adj f10,f13,f198,f205,f213,f217,f220,f230
  f230: cylinder r=0.2mm len=6.5mm, axis (0,0,1), area 2mm2, adj f198,f217,f229,f231
  f231: plane 6.5x0.8mm, normal (1,0,0), area 5.2mm2, adj f198,f217,f230,f232
  f232: cylinder r=0.5mm len=6.5mm, axis (0,0,1), area 5.1mm2, adj f198,f217,f231,f233
  f233: plane 6.5x0.75mm, normal (0,1,0), area 4.9mm2, adj f198,f217,f232,f234
  f234: cylinder r=0.5mm len=6.5mm, axis (0,0,1), area 5.1mm2, adj f198,f217,f233,f235
  f235: plane 6.5x0.8mm, normal (-1,0,0), area 5.2mm2, adj f198,f217,f234,f236
  f236: cylinder r=0.2mm len=6.5mm, axis (0,0,1), area 2mm2, adj f198,f217,f235,f237
  f237: plane 6.5x5.09mm, normal (0,1,0), area 31mm2, adj f193,f197,f198,f200,f216,f217,f223,f236
  f238: plane 6.5x5.09mm, normal (0,-1,0), area 31mm2, adj f2,f5,f8,f9,f202,f210,f221,f239
  f239: cylinder r=0.2mm len=6.5mm, axis (0,0,1), area 2mm2, adj f2,f5,f238,f240
  f240: plane 6.5x0.8mm, normal (-1,0,0), area 5.2mm2, adj f2,f5,f239,f241
  f241: cylinder r=0.5mm len=6.5mm, axis (0,0,1), area 5.1mm2, adj f2,f5,f224,f240
PLACE A at identity fixed
PLACE B t=(0,0,-23.35)mm
PLACE C t=(-0.07,0,-16.13)mm
MATE slider B.f3 <-> A.f25  axis (0,0,1) through (0,0,-19.4)mm
MATE slider A.f24 <-> C.f14  axis (0,0,1) through (0,0,27.75)mm
